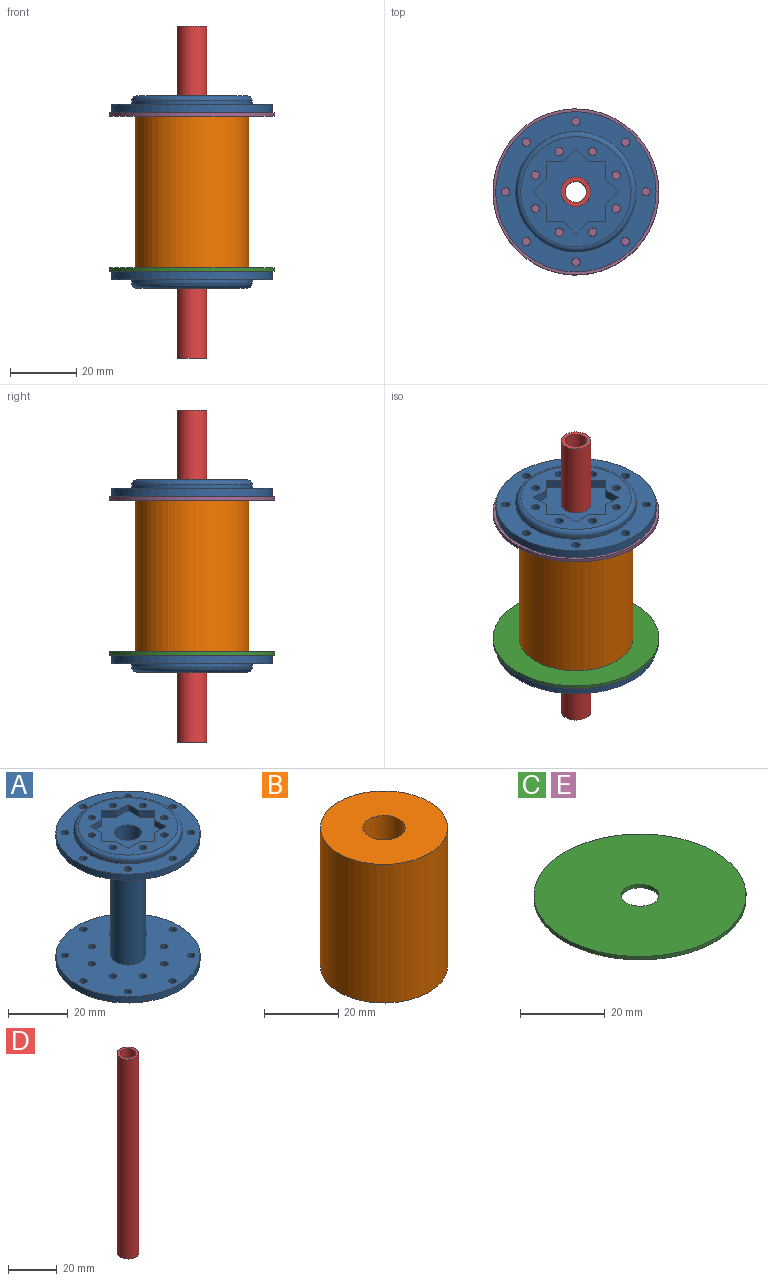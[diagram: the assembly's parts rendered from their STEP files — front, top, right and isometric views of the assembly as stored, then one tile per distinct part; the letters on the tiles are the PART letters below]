
ASSEMBLY  parts=5 mates=4
PART A: 80 faces, bbox 48.3x48.3x57.9 mm
  f0: cylinder r=4.45mm len=52.8mm, axis (0,0,-1), area 1474.6mm2, adj f43,f63
  f1: cylinder r=5.71mm len=47.72mm, axis (0,0,-1), area 1713.5mm2, adj f5,f7
  f2: plane 48.26x48.26mm, normal (0,0,1), area 757.3mm2, adj f4,f16,f17,f18,f19,f20,f21,f22
  f3: plane 48.26x48.26mm, normal (0,0,-1), area 757.3mm2, adj f6,f8,f9,f10,f11,f12,f13,f14
  f4: cylinder r=24.13mm len=48.26mm, axis (0,0,1), area 385.1mm2, adj f2,f5
  f5: plane 48.26x48.26mm, normal (0,0,-1), area 1648.1mm2, adj f1,f4,f16,f17,f18,f19,f20,f21
  f6: cylinder r=24.13mm len=48.26mm, axis (0,0,-1), area 385.1mm2, adj f3,f7
  f7: plane 48.26x48.26mm, normal (0,0,1), area 1648.1mm2, adj f1,f6,f8,f9,f10,f11,f12,f13
  f8: cylinder r=1.25mm len=2.54mm, axis (0,0,-1), area 19.9mm2, adj f3,f7
  f9: cylinder r=1.25mm len=2.54mm, axis (0,0,-1), area 19.9mm2, adj f3,f7
  f10: cylinder r=1.25mm len=2.54mm, axis (0,0,-1), area 19.9mm2, adj f3,f7
  f11: cylinder r=1.25mm len=2.54mm, axis (0,0,-1), area 19.9mm2, adj f3,f7
  f12: cylinder r=1.25mm len=2.54mm, axis (0,0,-1), area 19.9mm2, adj f3,f7
  f13: cylinder r=1.25mm len=2.54mm, axis (0,0,-1), area 19.9mm2, adj f3,f7
  f14: cylinder r=1.25mm len=2.54mm, axis (0,0,-1), area 19.9mm2, adj f3,f7
  f15: cylinder r=1.25mm len=2.54mm, axis (0,0,-1), area 19.9mm2, adj f3,f7
  f16: cylinder r=1.25mm len=2.54mm, axis (0,0,-1), area 19.9mm2, adj f2,f5
  f17: cylinder r=1.25mm len=2.54mm, axis (0,0,-1), area 19.9mm2, adj f2,f5
  f18: cylinder r=1.25mm len=2.54mm, axis (0,0,-1), area 19.9mm2, adj f2,f5
  f19: cylinder r=1.25mm len=2.54mm, axis (0,0,-1), area 19.9mm2, adj f2,f5
  f20: cylinder r=1.25mm len=2.54mm, axis (0,0,-1), area 19.9mm2, adj f2,f5
  f21: cylinder r=1.25mm len=2.54mm, axis (0,0,-1), area 19.9mm2, adj f2,f5
  f22: cylinder r=1.25mm len=2.54mm, axis (0,0,-1), area 19.9mm2, adj f2,f5
  f23: cylinder r=1.25mm len=2.54mm, axis (0,0,-1), area 19.9mm2, adj f2,f5
  f24: cylinder r=18.13mm len=36.26mm, axis (0,0,1), area 118.5mm2, adj f3,f26
  f25: plane 33.26x33.26mm, normal (0,0,-1), area 450mm2, adj f26,f27,f28,f29,f30,f31,f32,f33
  f26: torus R=16.63mm, axis (0,0,-1), area 260.3mm2, adj f24,f25
  f27: plane 3.73x3.73mm, normal (-0.71,0.71,0), area 13.4mm2, adj f25,f28,f42,f43
  f28: plane 5.27x2.54mm, normal (-1,0,0), area 13.4mm2, adj f25,f27,f29,f43
  f29: plane 5.27x2.54mm, normal (0,1,0), area 13.4mm2, adj f25,f28,f30,f43
  f30: plane 3.73x3.73mm, normal (-0.71,0.71,0), area 13.4mm2, adj f25,f29,f31,f43
  f31: plane 3.73x3.73mm, normal (0.71,0.71,0), area 13.4mm2, adj f25,f30,f32,f43
  f32: plane 5.27x2.54mm, normal (0,1,0), area 13.4mm2, adj f25,f31,f33,f43
  f33: plane 5.27x2.54mm, normal (1,0,0), area 13.4mm2, adj f25,f32,f34,f43
  f34: plane 3.73x3.73mm, normal (0.71,0.71,0), area 13.4mm2, adj f25,f33,f35,f43
  f35: plane 3.73x3.73mm, normal (0.71,-0.71,0), area 13.4mm2, adj f25,f34,f36,f43
  f36: plane 5.27x2.54mm, normal (1,0,0), area 13.4mm2, adj f25,f35,f37,f43
  f37: plane 5.27x2.54mm, normal (0,-1,0), area 13.4mm2, adj f25,f36,f38,f43
  f38: plane 3.73x3.73mm, normal (0.71,-0.71,0), area 13.4mm2, adj f25,f37,f39,f43
  f39: plane 3.73x3.73mm, normal (-0.71,-0.71,0), area 13.4mm2, adj f25,f38,f40,f43
  f40: plane 5.27x2.54mm, normal (0,-1,0), area 13.4mm2, adj f25,f39,f41,f43
  f41: plane 5.27x2.54mm, normal (-1,0,0), area 13.4mm2, adj f25,f40,f42,f43
  f42: plane 3.73x3.73mm, normal (-0.71,-0.71,0), area 13.4mm2, adj f25,f27,f41,f43
  f43: plane 25.46x25.46mm, normal (0,0,-1), area 317.5mm2, adj f0,f27,f28,f29,f30,f31,f32,f33
  f44: cylinder r=18.13mm len=36.26mm, axis (0,0,-1), area 118.5mm2, adj f2,f46
  f45: plane 33.26x33.26mm, normal (0,0,1), area 450mm2, adj f46,f47,f48,f49,f50,f51,f52,f53
  f46: torus R=16.63mm, axis (0,0,1), area 260.3mm2, adj f44,f45
  f47: plane 3.73x3.73mm, normal (-0.71,-0.71,0), area 13.4mm2, adj f45,f48,f62,f63
  f48: plane 5.27x2.54mm, normal (-1,0,0), area 13.4mm2, adj f45,f47,f49,f63
  f49: plane 5.27x2.54mm, normal (0,-1,0), area 13.4mm2, adj f45,f48,f50,f63
  f50: plane 3.73x3.73mm, normal (-0.71,-0.71,0), area 13.4mm2, adj f45,f49,f51,f63
  f51: plane 3.73x3.73mm, normal (0.71,-0.71,0), area 13.4mm2, adj f45,f50,f52,f63
  f52: plane 5.27x2.54mm, normal (0,-1,0), area 13.4mm2, adj f45,f51,f53,f63
  f53: plane 5.27x2.54mm, normal (1,0,0), area 13.4mm2, adj f45,f52,f54,f63
  f54: plane 3.73x3.73mm, normal (0.71,-0.71,0), area 13.4mm2, adj f45,f53,f55,f63
  f55: plane 3.73x3.73mm, normal (0.71,0.71,0), area 13.4mm2, adj f45,f54,f56,f63
  f56: plane 5.27x2.54mm, normal (1,0,0), area 13.4mm2, adj f45,f55,f57,f63
  f57: plane 5.27x2.54mm, normal (0,1,0), area 13.4mm2, adj f45,f56,f58,f63
  f58: plane 3.73x3.73mm, normal (0.71,0.71,0), area 13.4mm2, adj f45,f57,f59,f63
  f59: plane 3.73x3.73mm, normal (-0.71,0.71,0), area 13.4mm2, adj f45,f58,f60,f63
  f60: plane 5.27x2.54mm, normal (0,1,0), area 13.4mm2, adj f45,f59,f61,f63
  f61: plane 5.27x2.54mm, normal (-1,0,0), area 13.4mm2, adj f45,f60,f62,f63
  f62: plane 3.73x3.73mm, normal (-0.71,0.71,0), area 13.4mm2, adj f45,f47,f61,f63
  f63: plane 25.46x25.46mm, normal (0,0,1), area 317.5mm2, adj f0,f47,f48,f49,f50,f51,f52,f53
  f64: cylinder r=1.25mm len=5.08mm, axis (0,0,1), area 39.9mm2, adj f7,f25
  f65: cylinder r=1.25mm len=5.08mm, axis (0,0,1), area 39.9mm2, adj f7,f25
  f66: cylinder r=1.25mm len=5.08mm, axis (0,0,1), area 39.9mm2, adj f7,f25
  f67: cylinder r=1.25mm len=5.08mm, axis (0,0,1), area 39.9mm2, adj f7,f25
  f68: cylinder r=1.25mm len=5.08mm, axis (0,0,1), area 39.9mm2, adj f7,f25
  f69: cylinder r=1.25mm len=5.08mm, axis (0,0,1), area 39.9mm2, adj f7,f25
  f70: cylinder r=1.25mm len=5.08mm, axis (0,0,1), area 39.9mm2, adj f7,f25
  f71: cylinder r=1.25mm len=5.08mm, axis (0,0,1), area 39.9mm2, adj f7,f25
  f72: cylinder r=1.25mm len=5.08mm, axis (0,0,1), area 39.9mm2, adj f5,f45
  f73: cylinder r=1.25mm len=5.08mm, axis (0,0,1), area 39.9mm2, adj f5,f45
  f74: cylinder r=1.25mm len=5.08mm, axis (0,0,1), area 39.9mm2, adj f5,f45
  f75: cylinder r=1.25mm len=5.08mm, axis (0,0,1), area 39.9mm2, adj f5,f45
  f76: cylinder r=1.25mm len=5.08mm, axis (0,0,1), area 39.9mm2, adj f5,f45
  f77: cylinder r=1.25mm len=5.08mm, axis (0,0,1), area 39.9mm2, adj f5,f45
  f78: cylinder r=1.25mm len=5.08mm, axis (0,0,1), area 39.9mm2, adj f5,f45
  f79: cylinder r=1.25mm len=5.08mm, axis (0,0,1), area 39.9mm2, adj f5,f45
PART B: 4 faces, bbox 34.3x34.3x45.7 mm
  f0: cylinder r=5.71mm len=45.72mm, axis (0,0,-1), area 1641.7mm2, adj f2,f3
  f1: cylinder r=17.14mm len=45.72mm, axis (0,0,-1), area 4925.2mm2, adj f2,f3
  f2: plane 34.29x34.29mm, normal (0,0,1), area 820.9mm2, adj f0,f1
  f3: plane 34.29x34.29mm, normal (0,0,-1), area 820.9mm2, adj f0,f1
PART C: 4 faces, bbox 50x50x1 mm
  f0: cylinder r=4.45mm len=8.9mm, axis (0,0,-1), area 28mm2, adj f2,f3
  f1: cylinder r=25mm len=50mm, axis (0,0,-1), area 157.1mm2, adj f2,f3
  f2: plane 50x50mm, normal (0,0,1), area 1901.3mm2, adj f0,f1
  f3: plane 50x50mm, normal (0,0,-1), area 1901.3mm2, adj f0,f1
PART D: 4 faces, bbox 8.9x8.9x100 mm
  f0: cylinder r=3.17mm len=100mm, axis (0,0,-1), area 1994.9mm2, adj f2,f3
  f1: cylinder r=4.45mm len=100mm, axis (0,0,-1), area 2792.9mm2, adj f2,f3
  f2: plane 8.89x8.89mm, normal (0,0,1), area 30.4mm2, adj f0,f1
  f3: plane 8.89x8.89mm, normal (0,0,-1), area 30.4mm2, adj f0,f1
PART E: same geometry as C
PLACE A t=(22.19,18.21,-5.89)mm
PLACE B rot(axis=(1,0,0),180deg) t=(22.19,18.21,43.37)mm
PLACE C t=(22.19,18.21,-3.35)mm
PLACE D t=(22.19,18.21,-29.49)mm
PLACE E t=(22.19,18.21,43.37)mm
MATE revolute E.f0 <-> A.f1  axis (0,0,1) through (22.19,18.21,44.37)mm
MATE fastened B.f0 <-> C.f0  axis (0,0,1) through (22.19,18.21,-2.35)mm
MATE cylindrical D.f0 <-> A.f0  axis (0,0,-1) through (22.19,18.21,20.51)mm
MATE fastened B.f0 <-> E.f0  axis (0,0,1) through (22.19,18.21,43.37)mm
